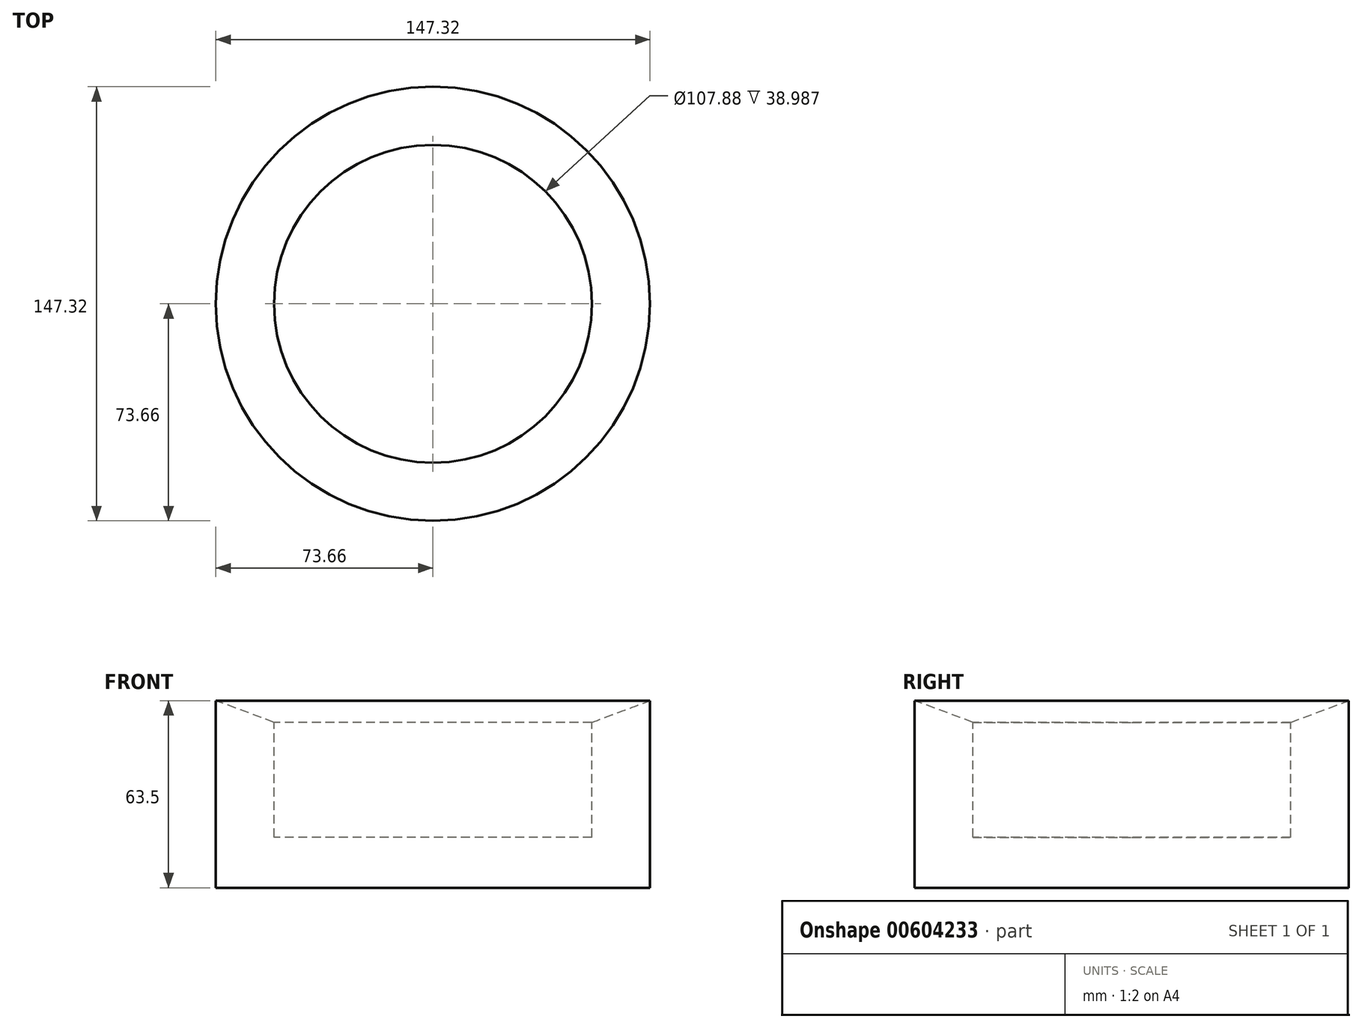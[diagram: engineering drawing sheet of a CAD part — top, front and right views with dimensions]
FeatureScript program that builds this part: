
annotation { "Feature Type Name" : "Feature", "Feature Type Description" : "" }
export const myFeature = defineFeature(function(context is Context, id is Id, definition is map)
    precondition{}
    {
        {
            var Q0;
            Q0=qCreatedBy(makeId("Front.planeOp"),FACE);
            var sketch = newSketch(context, id + "F0", { "sketchPlane" : qUnion([Q0])});
            skLineSegment(sketch, "E0", {"start": v(-73.66, 63.5) * mm, "end": v(-53.94, 56.13) * mm});
            skLineSegment(sketch, "E1", {"start": v(-53.94, 56.13) * mm, "end": v(-53.94, 17.15) * mm});
            skLineSegment(sketch, "E2", {"start": v(-53.94, 17.15) * mm, "end": v(0, 17.15) * mm});
            skLineSegment(sketch, "E3", {"start": v(0, 17.15) * mm, "end": v(0, 0) * mm});
            skLineSegment(sketch, "E4", {"start": v(0, 0) * mm, "end": v(-73.66, 0) * mm});
            skLineSegment(sketch, "E5", {"start": v(-73.66, 0) * mm, "end": v(-73.66, 63.5) * mm});
            skSolve(sketch);
        }
        {
            var Q0;
            Q0=makeQuery(id+"F0.imprint","IMPRINT",FACE,{"disambiguationData":[TD([[makeQuery(id+"F0.imprint","IMPRINT",EDGE,{"derivedFrom":sQuery(id+"F0.wireOp",EDGE,"E0")}),-1.0]])]});
            var Q1;
            Q1=sQuery(id+"F0.wireOp",EDGE,"E3");
            revolve(context, id + "F1", {"entities" : qUnion([Q0]), "axis" : qUnion([Q1]), "revolveType" : RevolveType.FULL});
        }
    });
